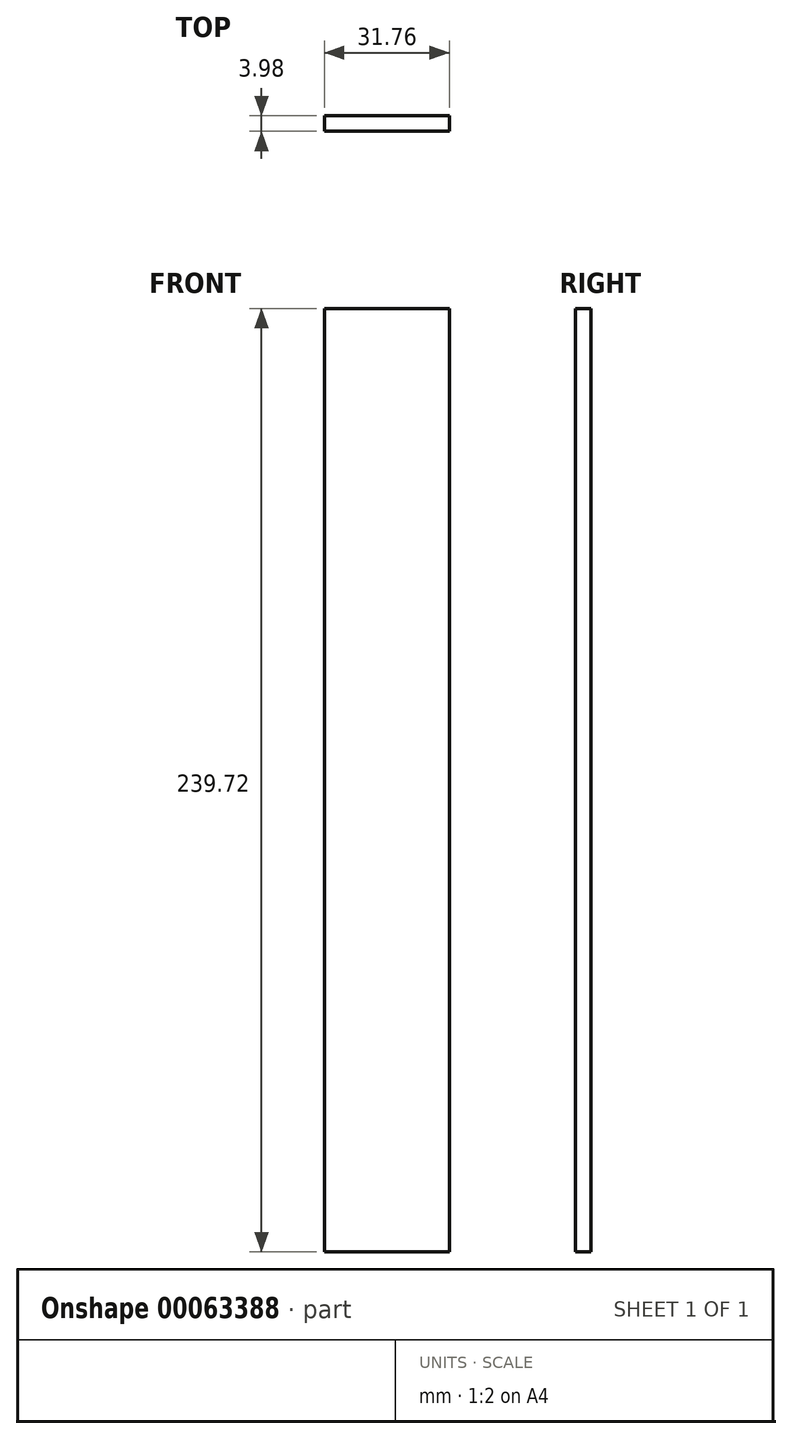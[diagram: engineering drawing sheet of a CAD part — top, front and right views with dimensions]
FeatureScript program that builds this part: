
annotation { "Feature Type Name" : "Feature", "Feature Type Description" : "" }
export const myFeature = defineFeature(function(context is Context, id is Id, definition is map)
    precondition{}
    {
        {
            var Q0;
            Q0=qCreatedBy(makeId("Top.planeOp"),FACE);
            var sketch = newSketch(context, id + "F0", { "sketchPlane" : qUnion([Q0])});
            skLineSegment(sketch, "E0.rect.bottom", {"start": v(15.87, 2) * mm, "end": v(-15.88, 2) * mm});
            skLineSegment(sketch, "E0.rect.top", {"start": v(15.87, -2) * mm, "end": v(-15.88, -2) * mm});
            skLineSegment(sketch, "E0.rect.left", {"start": v(15.87, 2) * mm, "end": v(15.87, -2) * mm});
            skLineSegment(sketch, "E0.rect.right", {"start": v(-15.88, 2) * mm, "end": v(-15.88, -2) * mm});
            skPoint(sketch, "E0.rect.middle", {"position": v(0, 0) * mm});
            skSolve(sketch);
        }
        {
            var Q0;
            Q0=qSketchRegion(id+"F0",true);
            extrude(context, id + "F1", {"entities" : qUnion([Q0]), "endBound" : BoundingType.SYMMETRIC, "depth" : 239.72 * mm});
        }
    });
